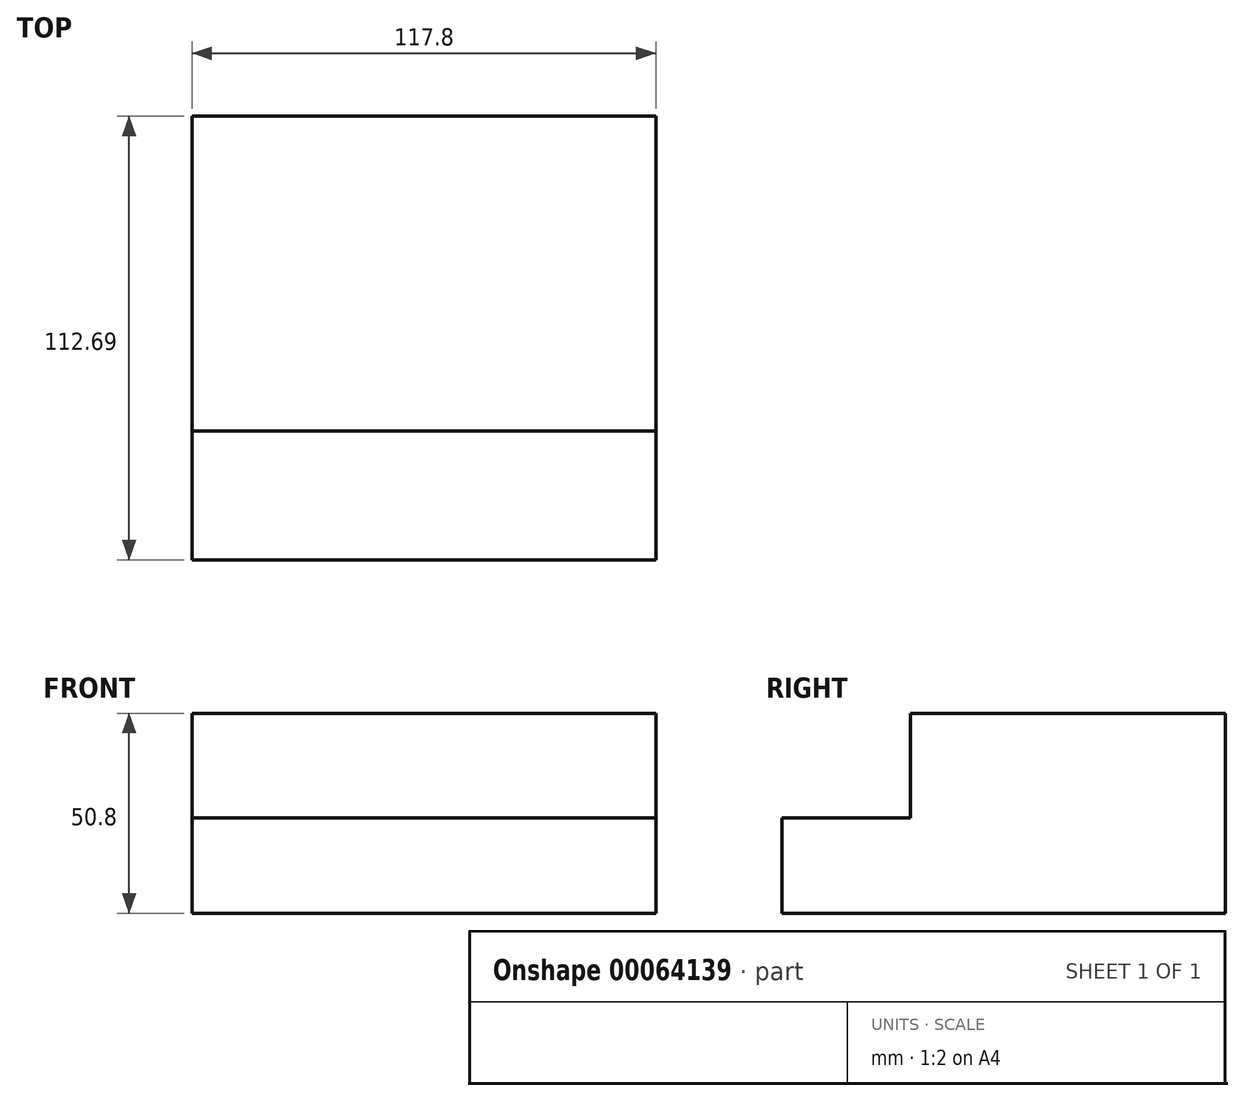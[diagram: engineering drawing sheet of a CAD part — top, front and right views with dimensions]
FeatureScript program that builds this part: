
annotation { "Feature Type Name" : "Feature", "Feature Type Description" : "" }
export const myFeature = defineFeature(function(context is Context, id is Id, definition is map)
    precondition{}
    {
        {
            var Q0;
            Q0=qCreatedBy(makeId("Top.planeOp"),FACE);
            var sketch = newSketch(context, id + "F0", { "sketchPlane" : qUnion([Q0])});
            skLineSegment(sketch, "E0.bottom", {"start": v(-75.5, -75.28) * mm, "end": v(42.3, -75.28) * mm});
            skLineSegment(sketch, "E0.top", {"start": v(-75.5, 37.4) * mm, "end": v(42.3, 37.4) * mm});
            skLineSegment(sketch, "E0.left", {"start": v(-75.5, -75.28) * mm, "end": v(-75.5, 37.4) * mm});
            skLineSegment(sketch, "E0.right", {"start": v(42.3, -75.28) * mm, "end": v(42.3, 37.4) * mm});
            skSolve(sketch);
        }
        {
            var Q0;
            Q0=makeQuery(id+"F0.imprint","IMPRINT",FACE,{"disambiguationData":[TD([[makeQuery(id+"F0.imprint","IMPRINT",EDGE,{"derivedFrom":sQuery(id+"F0.wireOp",EDGE,"E0.bottom")}),1.0]])]});
            extrude(context, id + "F1", {"entities" : qUnion([Q0]), "depth" : 50.8 * mm});
        }
        {
            var Q0;
            Q0=makeQuery(id+"F1.opExtrude","SWEPT_FACE",FACE,{"disambiguationData":[OSD([sQuery(id+"F0.wireOp",EDGE,"E0.right")])]});
            var sketch = newSketch(context, id + "F2", { "sketchPlane" : qUnion([Q0])});
            skLineSegment(sketch, "E1.bottom", {"start": v(-75.28, 50.8) * mm, "end": v(-42.55, 50.8) * mm});
            skLineSegment(sketch, "E1.top", {"start": v(-75.28, 24.22) * mm, "end": v(-42.55, 24.22) * mm});
            skLineSegment(sketch, "E1.left", {"start": v(-75.28, 50.8) * mm, "end": v(-75.28, 24.22) * mm});
            skLineSegment(sketch, "E1.right", {"start": v(-42.55, 50.8) * mm, "end": v(-42.55, 24.22) * mm});
            skSolve(sketch);
        }
        {
            var Q0;
            Q0=makeQuery(id+"F2.imprint","IMPRINT",FACE,{"disambiguationData":[TD([[makeQuery(id+"F2.imprint","IMPRINT",EDGE,{"derivedFrom":sQuery(id+"F2.wireOp",EDGE,"E1.bottom")}),-1.0]])]});
            extrude(context, id + "F3", {"entities" : qUnion([Q0]), "operationType" : NewBodyOperationType.REMOVE, "oppositeDirection" : true, "depth" : 151.4 * mm});
        }
    });
